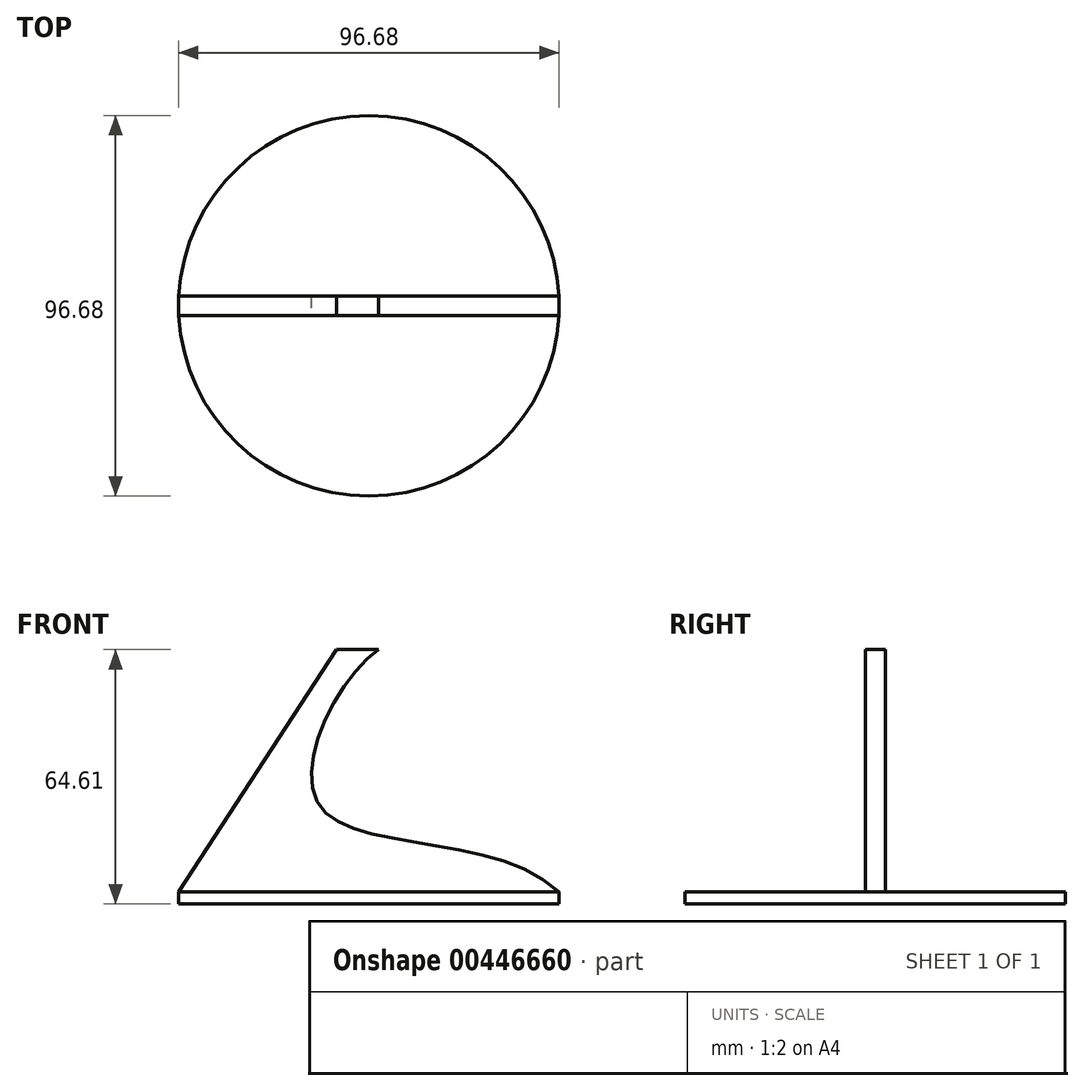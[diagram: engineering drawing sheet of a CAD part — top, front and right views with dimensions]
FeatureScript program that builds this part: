
annotation { "Feature Type Name" : "Feature", "Feature Type Description" : "" }
export const myFeature = defineFeature(function(context is Context, id is Id, definition is map)
    precondition{}
    {
        {
            var Q0;
            Q0=qCreatedBy(makeId("Front.planeOp"),FACE);
            var sketch = newSketch(context, id + "F0", { "sketchPlane" : qUnion([Q0])});
            skLineSegment(sketch, "E0", {"start": v(10.62, 40.55) * mm, "end": v(0, 40.55) * mm});
            skLineSegment(sketch, "E1", {"start": v(0, 40.55) * mm, "end": v(-40.1, -21.06) * mm});
            skLineSegment(sketch, "E2", {"start": v(-40.1, -21.06) * mm, "end": v(56.45, -21.06) * mm});
            skFitSpline(sketch, "E3", {"points": [v(10.62, 40.55) * mm, v(-4.48, 1.1) * mm, v(56.45, -21.06) * mm], "startDerivative": vector(-67.02, -46.31) * mm, "endDerivative": vector(85.8, -84) * mm});
            skSolve(sketch);
        }
        {
            var Q0;
            Q0 = qSketchRegion(id + "F0", true);
            extrude(context, id + "F1", {"entities" : qUnion([Q0]), "depth" : 5 * mm});
        }
        {
            var Q0;
            Q0=makeQuery(id+"F1.opExtrude","SWEPT_FACE",FACE,{"disambiguationData":[OSD([sQuery(id+"F0.wireOp",EDGE,"E2")])]});
            var sketch = newSketch(context, id + "F2", { "sketchPlane" : qUnion([Q0])});
            skLineSegment(sketch, "E4", {"start": v(8.18, 5) * mm, "end": v(8.18, 0) * mm, "construction": true});
            skCircle(sketch, "E5", {"center": v(8.18, 2.5) * mm, "radius": 48.34 * mm});
            skSolve(sketch);
        }
        {
            var Q0;
            Q0 = qSketchRegion(id + "F2", true);
            var Q1;
            Q1 = qConstructionFilter(qBodyType(qCreatedBy(id + "F2" ,EDGE), BodyType.WIRE), ConstructionObject.NO);
            extrude(context, id + "F3", {"entities" : qUnion([Q0]), "operationType" : NewBodyOperationType.ADD, "surfaceEntities" : qUnion([Q1]), "depth" : 3 * mm});
        }
    });
